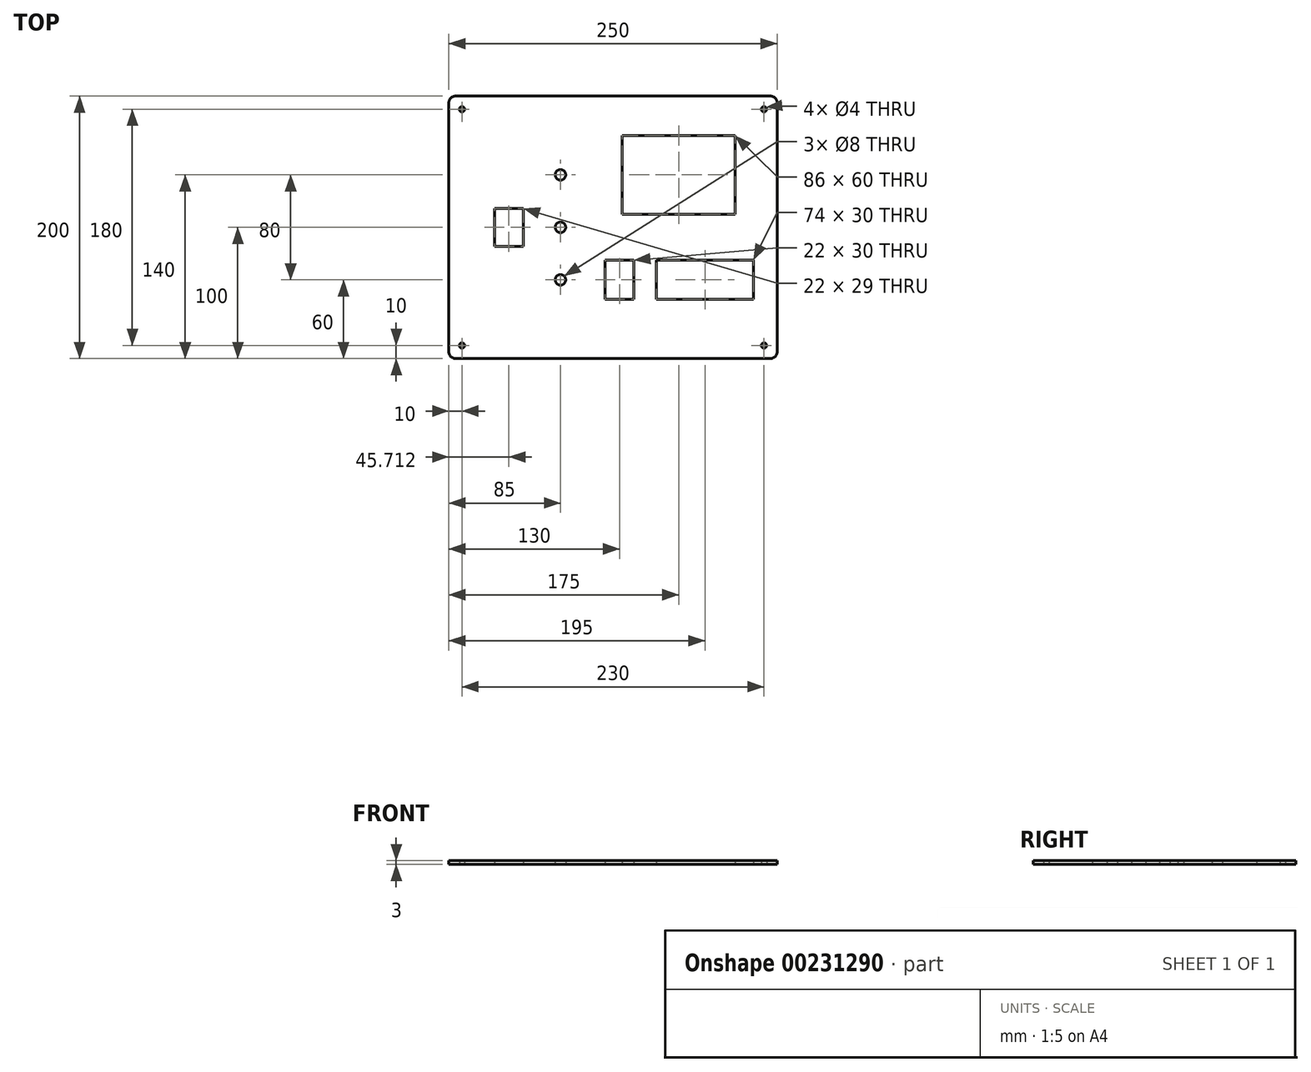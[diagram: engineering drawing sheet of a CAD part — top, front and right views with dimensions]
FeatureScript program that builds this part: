
annotation { "Feature Type Name" : "Feature", "Feature Type Description" : "" }
export const myFeature = defineFeature(function(context is Context, id is Id, definition is map)
    precondition{}
    {
        {
            var Q0;
            Q0=qCreatedBy(makeId("Top.planeOp"),FACE);
            var sketch = newSketch(context, id + "F0", { "sketchPlane" : qUnion([Q0])});
            skLineSegment(sketch, "E0.bottom", {"start": v(120, -100) * mm, "end": v(-120, -100) * mm});
            skLineSegment(sketch, "E0.top", {"start": v(120, 100) * mm, "end": v(-120, 100) * mm});
            skLineSegment(sketch, "E0.left", {"start": v(125, -95) * mm, "end": v(125, 95) * mm});
            skLineSegment(sketch, "E0.right", {"start": v(-125, -95) * mm, "end": v(-125, 95) * mm});
            skPoint(sketch, "E0.middle", {"position": v(0, 0) * mm});
            skCircle(sketch, "E1", {"center": v(-40, 40) * mm, "radius": 4 * mm});
            skCircle(sketch, "E2", {"center": v(-40, 0) * mm, "radius": 4 * mm});
            skCircle(sketch, "E3", {"center": v(-40, -40) * mm, "radius": 4 * mm});
            skLineSegment(sketch, "E4", {"start": v(-134.5, 0) * mm, "end": v(54.5, 0) * mm, "construction": true});
            skPoint(sketch, "E4.startSnap0", {"position": v(-125, 0) * mm});
            skPoint(sketch, "E4.endSnap0", {"position": v(125, 0) * mm});
            skLineSegment(sketch, "E5.bottom", {"start": v(93, 10) * mm, "end": v(7, 10) * mm});
            skLineSegment(sketch, "E5.top", {"start": v(93, 70) * mm, "end": v(7, 70) * mm});
            skLineSegment(sketch, "E5.left", {"start": v(93, 10) * mm, "end": v(93, 70) * mm});
            skLineSegment(sketch, "E5.right", {"start": v(7, 10) * mm, "end": v(7, 70) * mm});
            skPoint(sketch, "E5.middle", {"position": v(50, 40) * mm});
            skLineSegment(sketch, "E6.bottom", {"start": v(107, -55) * mm, "end": v(33, -55) * mm});
            skLineSegment(sketch, "E6.top", {"start": v(107, -25) * mm, "end": v(33, -25) * mm});
            skLineSegment(sketch, "E6.left", {"start": v(107, -55) * mm, "end": v(107, -25) * mm});
            skLineSegment(sketch, "E6.right", {"start": v(33, -55) * mm, "end": v(33, -25) * mm});
            skPoint(sketch, "E6.middle", {"position": v(70, -40) * mm});
            skPoint(sketch, "E6.middle.positionSnap0", {"position": v(50, 10) * mm});
            skPoint(sketch, "E6.centerSnap0", {"position": v(50, 10) * mm});
            skLineSegment(sketch, "E7.bottom", {"start": v(16, -55) * mm, "end": v(-6, -55) * mm});
            skLineSegment(sketch, "E7.top", {"start": v(16, -25) * mm, "end": v(-6, -25) * mm});
            skLineSegment(sketch, "E7.left", {"start": v(16, -55) * mm, "end": v(16, -25) * mm});
            skLineSegment(sketch, "E7.right", {"start": v(-6, -55) * mm, "end": v(-6, -25) * mm});
            skPoint(sketch, "E7.middle", {"position": v(5, -40) * mm});
            skPoint(sketch, "E7.middle.positionSnap0", {"position": v(33, -40) * mm});
            skPoint(sketch, "E7.centerSnap0", {"position": v(33, -40) * mm});
            skLineSegment(sketch, "E8.bottom", {"start": v(108, -57) * mm, "end": v(32, -57) * mm, "construction": true});
            skLineSegment(sketch, "E8.top", {"start": v(108, -23) * mm, "end": v(32, -23) * mm, "construction": true});
            skLineSegment(sketch, "E8.left", {"start": v(108, -57) * mm, "end": v(108, -23) * mm, "construction": true});
            skLineSegment(sketch, "E8.right", {"start": v(32, -57) * mm, "end": v(32, -23) * mm, "construction": true});
            skLineSegment(sketch, "E9.bottom", {"start": v(17.5, -56) * mm, "end": v(-7.5, -56) * mm, "construction": true});
            skLineSegment(sketch, "E9.top", {"start": v(17.5, -24) * mm, "end": v(-7.5, -24) * mm, "construction": true});
            skLineSegment(sketch, "E9.left", {"start": v(17.5, -56) * mm, "end": v(17.5, -24) * mm, "construction": true});
            skLineSegment(sketch, "E9.right", {"start": v(-7.5, -56) * mm, "end": v(-7.5, -24) * mm, "construction": true});
            skLineSegment(sketch, "E10.bottom", {"start": v(104.5, 0) * mm, "end": v(-4.5, 0) * mm, "construction": true});
            skLineSegment(sketch, "E10.top", {"start": v(104.5, 80) * mm, "end": v(-4.5, 80) * mm, "construction": true});
            skLineSegment(sketch, "E10.left", {"start": v(104.5, 0) * mm, "end": v(104.5, 80) * mm, "construction": true});
            skLineSegment(sketch, "E10.right", {"start": v(-4.5, 0) * mm, "end": v(-4.5, 80) * mm, "construction": true});
            skLineSegment(sketch, "E11.bottom", {"start": v(-68.29, -14.5) * mm, "end": v(-90.29, -14.5) * mm});
            skLineSegment(sketch, "E11.top", {"start": v(-68.29, 14.5) * mm, "end": v(-90.29, 14.5) * mm});
            skLineSegment(sketch, "E11.left", {"start": v(-68.29, -14.5) * mm, "end": v(-68.29, 14.5) * mm});
            skLineSegment(sketch, "E11.right", {"start": v(-90.29, -14.5) * mm, "end": v(-90.29, 14.5) * mm});
            skPoint(sketch, "E11.middle", {"position": v(-79.29, 0) * mm});
            skLineSegment(sketch, "E12.bottom", {"start": v(-66.79, -16) * mm, "end": v(-91.79, -16) * mm, "construction": true});
            skLineSegment(sketch, "E12.top", {"start": v(-66.79, 16) * mm, "end": v(-91.79, 16) * mm, "construction": true});
            skLineSegment(sketch, "E12.left", {"start": v(-66.79, -16) * mm, "end": v(-66.79, 16) * mm, "construction": true});
            skLineSegment(sketch, "E12.right", {"start": v(-91.79, -16) * mm, "end": v(-91.79, 16) * mm, "construction": true});
            skPoint(sketch, "E13.centerSnap0", {"position": v(7, 40) * mm});
            skPoint(sketch, "E13.perimeterSnap0", {"position": v(7, 40) * mm});
            skPoint(sketch, "E14.visualSharp", {"position": v(-125, 100) * mm});
            skArc(sketch, "E14.filletArc", {"start": v(-120, 100) * mm, "mid": v(-123.54, 98.54) * mm, "end": v(-125, 95) * mm});
            skPoint(sketch, "E15.visualSharp", {"position": v(125, 100) * mm});
            skArc(sketch, "E15.filletArc", {"start": v(125, 95) * mm, "mid": v(123.54, 98.54) * mm, "end": v(120, 100) * mm});
            skPoint(sketch, "E16.visualSharp", {"position": v(-125, -100) * mm});
            skArc(sketch, "E16.filletArc", {"start": v(-125, -95) * mm, "mid": v(-123.54, -98.54) * mm, "end": v(-120, -100) * mm});
            skPoint(sketch, "E17.visualSharp", {"position": v(125, -100) * mm});
            skArc(sketch, "E17.filletArc", {"start": v(120, -100) * mm, "mid": v(123.54, -98.54) * mm, "end": v(125, -95) * mm});
            skCircle(sketch, "E18", {"center": v(-115, 90) * mm, "radius": 2 * mm});
            skCircle(sketch, "E19", {"center": v(115, 90) * mm, "radius": 2 * mm});
            skCircle(sketch, "E20", {"center": v(-115, -90) * mm, "radius": 2 * mm});
            skCircle(sketch, "E21", {"center": v(115, -90) * mm, "radius": 2 * mm});
            skSolve(sketch);
        }
        {
            var Q0;
            Q0=makeQuery(id+"F0.imprint","IMPRINT",FACE,{"disambiguationData":[TD([[makeQuery(id+"F0.imprint","IMPRINT",EDGE,{"derivedFrom":sQuery(id+"F0.wireOp",EDGE,"E0.bottom")}),-1.0]])]});
            extrude(context, id + "F1", {"entities" : qUnion([Q0]), "depth" : 3 * mm});
        }
    });
